# Revit family: Haworth_ComposeStorage_Top
name_source: partatom
category: Furniture Systems
revit_build: Autodesk Revit 2018 (Build: 20170223_1515(x64)
units: mm (PartAtom-declared; Revit-internal decimal feet)

## family parameters
Always vertical = Yes
Cut with Voids When Loaded = No
OmniClass Number = 23.40.70.14.64.21
OmniClass Title = Systems Furniture
Part Type = Normal
Room Calculation Point = No
Round Connector Dimension = Use Diameter
Shared = No
Work Plane-Based = No

## types (96) — shared parameters
Assembly Code = E2020200
Description = Haworth - Compose Storage Top
Edge Finish = Haworth _ Wood _ White Oak
Manufacturer = Haworth
Max. Depth = 48"
Max. Width = 108"
Min. Depth = 18"
Min. Width = 16"
Min/Max Depth = 18-48 in.
Min/Max Width = 16-108 in.
Model = BZT
Revision Number = 5
Size = Verify Final Dim. w/ Haworth
Sustainability Info = http://media.haworth.com
Top Finish = Haworth _ Wood _ White Oak
Top Thickness = 1 3/16"
URL = www.haworth.com
URL - Product = http://www.haworth.com
Warranty = http://www.haworth.com

## per-type parameters (varying)
| type | Actual Depth | Actual Width | Depth | Width |
| 18w 18d | 18" | 18" | 18" | 18" |
| 24w 18d | 18" | 24" | 18" | 24" |
| 30w 18d | 18" | 30" | 18" | 30" |
| 36w 18d | 18" | 36" | 18" | 36" |
| 42w 18d | 18" | 42" | 18" | 42" |
| 48w 18d | 18" | 48" | 18" | 48" |
| 54w 18d | 18" | 54" | 18" | 54" |
| 60w 18d | 18" | 60" | 18" | 60" |
| 66w 18d | 18" | 66" | 18" | 66" |
| 72w 18d | 18" | 72" | 18" | 72" |
| 78w 18d | 18" | 78" | 18" | 78" |
| 84w 18d | 18" | 84" | 18" | 84" |
| 90w 18d | 18" | 90" | 18" | 90" |
| 96w 18d | 18" | 96" | 18" | 96" |
| 102w 18d | 18" | 102" | 18" | 102" |
| 108w 18d | 18" | 108" | 18" | 108" |
| 18w 24d | 24" | 18" | 24" | 18" |
| 24w 24d | 24" | 24" | 24" | 24" |
| 30w 24d | 24" | 30" | 24" | 30" |
| 36w 24d | 24" | 36" | 24" | 36" |
| 42w 24d | 24" | 42" | 24" | 42" |
| 48w 24d | 24" | 48" | 24" | 48" |
| 54w 24d | 24" | 54" | 24" | 54" |
| 60w 24d | 24" | 60" | 24" | 60" |
| 66w 24d | 24" | 66" | 24" | 66" |
| 72w 24d | 24" | 72" | 24" | 72" |
| 78w 24d | 24" | 78" | 24" | 78" |
| 84w 24d | 24" | 84" | 24" | 84" |
| 90w 24d | 24" | 90" | 24" | 90" |
| 96w 24d | 24" | 96" | 24" | 96" |
| 102w 24d | 24" | 102" | 24" | 102" |
| 108w 24d | 24" | 108" | 24" | 108" |
| 18w 30d | 30" | 18" | 30" | 18" |
| 24w 30d | 30" | 24" | 30" | 24" |
| 30w 30d | 30" | 30" | 30" | 30" |
| 36w 30d | 30" | 36" | 30" | 36" |
| 42w 30d | 30" | 42" | 30" | 42" |
| 48w 30d | 30" | 48" | 30" | 48" |
| 54w 30d | 30" | 54" | 30" | 54" |
| 60w 30d | 30" | 60" | 30" | 60" |
| 66w 30d | 30" | 66" | 30" | 66" |
| 72w 30d | 30" | 72" | 30" | 72" |
| 78w 30d | 30" | 78" | 30" | 78" |
| 84w 30d | 30" | 84" | 30" | 84" |
| 90w 30d | 30" | 90" | 30" | 90" |
| 96w 30d | 30" | 96" | 30" | 96" |
| 102w 30d | 30" | 102" | 30" | 102" |
| 108w 30d | 30" | 108" | 30" | 108" |
| 18w 36d | 36" | 18" | 36" | 18" |
| 24w 36d | 36" | 24" | 36" | 24" |
| 30w 36d | 36" | 30" | 36" | 30" |
| 36w 36d | 36" | 36" | 36" | 36" |
| 42w 36d | 36" | 42" | 36" | 42" |
| 48w 36d | 36" | 48" | 36" | 48" |
| 54w 36d | 36" | 54" | 36" | 54" |
| 60w 36d | 36" | 60" | 36" | 60" |
| 66w 36d | 36" | 66" | 36" | 66" |
| 72w 36d | 36" | 72" | 36" | 72" |
| 78w 36d | 36" | 78" | 36" | 78" |
| 84w 36d | 36" | 84" | 36" | 84" |
| 90w 36d | 36" | 90" | 36" | 90" |
| 96w 36d | 36" | 96" | 36" | 96" |
| 102w 36d | 36" | 102" | 36" | 102" |
| 108w 36d | 36" | 108" | 36" | 108" |
| 18w 42d | 42" | 18" | 42" | 18" |
| 24w 42d | 42" | 24" | 42" | 24" |
| 30w 42d | 42" | 30" | 42" | 30" |
| 36w 42d | 42" | 36" | 42" | 36" |
| 42w 42d | 42" | 42" | 42" | 42" |
| 48w 42d | 42" | 48" | 42" | 48" |
| 54w 42d | 42" | 54" | 42" | 54" |
| 60w 42d | 42" | 60" | 42" | 60" |
| 66w 42d | 42" | 66" | 42" | 66" |
| 72w 42d | 42" | 72" | 42" | 72" |
| 78w 42d | 42" | 78" | 42" | 78" |
| 84w 42d | 42" | 84" | 42" | 84" |
| 90w 42d | 42" | 90" | 42" | 90" |
| 96w 42d | 42" | 96" | 42" | 96" |
| 102w 42d | 42" | 102" | 42" | 102" |
| 108w 42d | 42" | 108" | 42" | 108" |
| 18w 48d | 48" | 18" | 48" | 18" |
| 24w 48d | 48" | 24" | 48" | 24" |
| 30w 48d | 48" | 30" | 48" | 30" |
| 36w 48d | 48" | 36" | 48" | 36" |
| 42w 48d | 48" | 42" | 48" | 42" |
| 48w 48d | 48" | 48" | 48" | 48" |
| 54w 48d | 48" | 54" | 48" | 54" |
| 60w 48d | 48" | 60" | 48" | 60" |
| 66w 48d | 48" | 66" | 48" | 66" |
| 72w 48d | 48" | 72" | 48" | 72" |
| 78w 48d | 48" | 78" | 48" | 78" |
| 84w 48d | 48" | 84" | 48" | 84" |
| 90w 48d | 48" | 90" | 48" | 90" |
| 96w 48d | 48" | 96" | 48" | 96" |
| 102w 48d | 48" | 102" | 48" | 102" |
| 108w 48d | 48" | 108" | 48" | 108" |

## geometry (parser evidence)
native form markers: Sweep x3
no freeform markers — native parametric forms only
